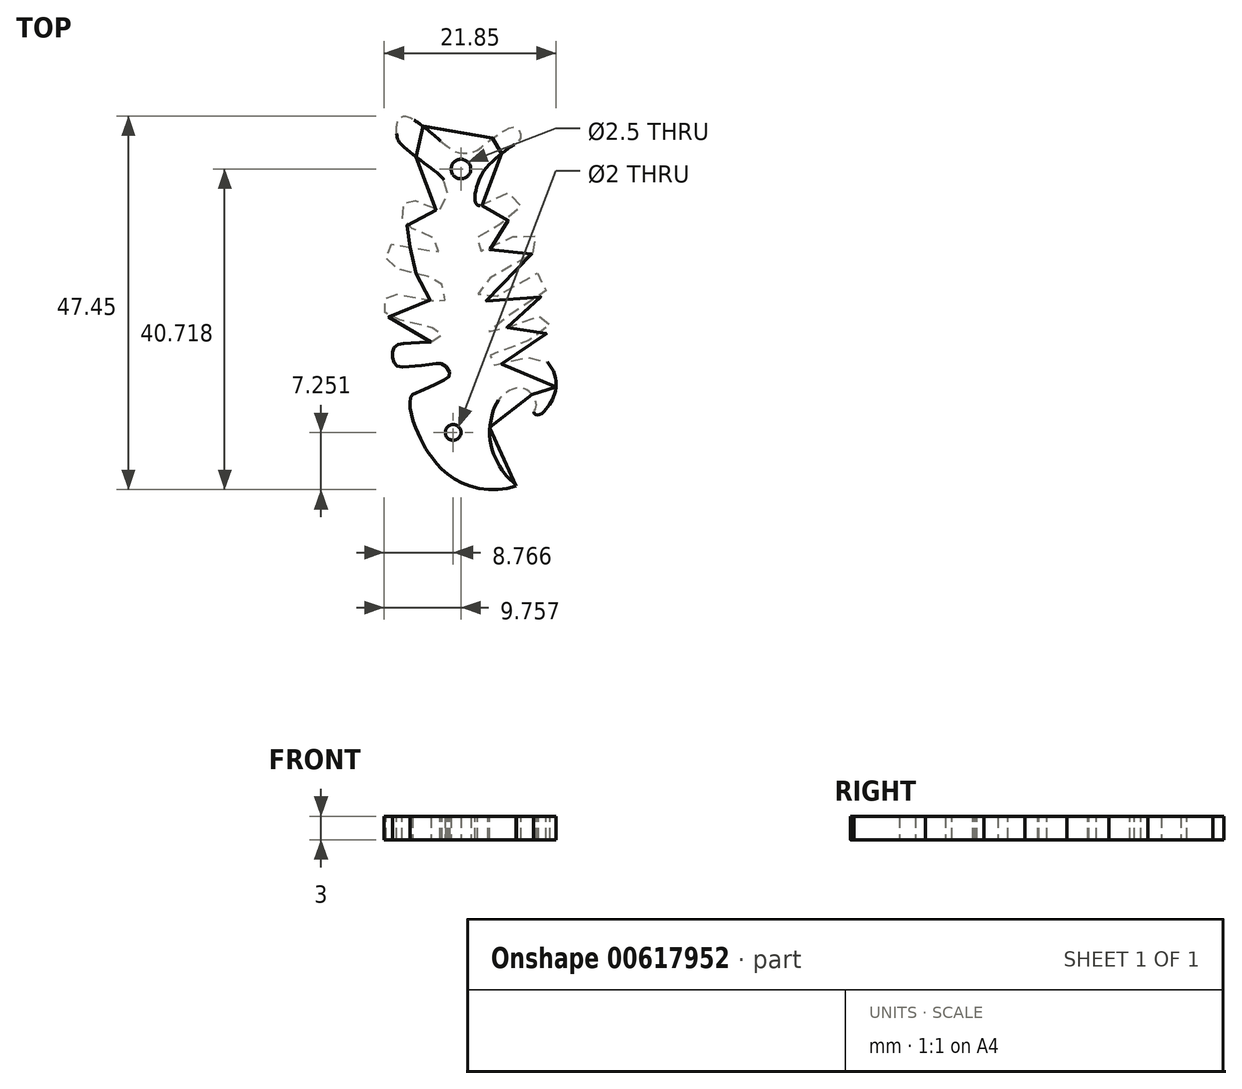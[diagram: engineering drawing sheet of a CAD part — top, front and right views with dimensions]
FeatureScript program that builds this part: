
annotation { "Feature Type Name" : "Feature", "Feature Type Description" : "" }
export const myFeature = defineFeature(function(context is Context, id is Id, definition is map)
    precondition{}
    {
        {
            var Q0;
            Q0=qCreatedBy(makeId("Top.planeOp"),FACE);
            var sketch = newSketch(context, id + "F0", { "sketchPlane" : qUnion([Q0])});
            skFitSpline(sketch, "E0", {"points": [v(6.13, -20.14) * mm, v(-0.93, -19.67) * mm, v(-4.7, -16.3) * mm, v(-6.1, -13.93) * mm, v(-7.28, -10.5) * mm, v(-7.02, -8.5) * mm], "startDerivative": vector(-25.08, -8.24) * mm, "endDerivative": vector(7.76, 5.26) * mm});
            skFitSpline(sketch, "E1", {"points": [v(-7.02, -8.5) * mm, v(-2.72, -6.48) * mm, v(-2.28, -5.84) * mm, v(-3.08, -4.7) * mm, v(-4.22, -4.59) * mm, v(-6.24, -4.86) * mm, v(-7.67, -4.96) * mm, v(-9.04, -4.88) * mm, v(-9.5, -4.1) * mm, v(-9.54, -3.1) * mm, v(-9.16, -2.31) * mm, v(-7.99, -2) * mm, v(-4.66, -1.85) * mm], "startDerivative": vector(31.33, 13.7) * mm, "endDerivative": vector(38.08, 1.18) * mm});
            skFitSpline(sketch, "E2", {"points": [v(-4.66, -1.85) * mm, v(-3.6, -1.52) * mm, v(-3.29, -0.77) * mm, v(-3.8, -0.25) * mm, v(-4.66, 0) * mm, v(-9.7, 1.25) * mm, v(-10.44, 1.63) * mm, v(-10.61, 2.48) * mm, v(-10.55, 3.42) * mm, v(-10.06, 4.3) * mm, v(-9, 4.25) * mm, v(-3.9, 3.3) * mm, v(-3.3, 3.21) * mm, v(-2.83, 3.57) * mm, v(-2.91, 4.8) * mm, v(-3.73, 5.97) * mm, v(-4.96, 6.47) * mm, v(-9.46, 7.6) * mm, v(-10.28, 8.27) * mm, v(-10.32, 9.72) * mm, v(-9.74, 10.6) * mm, v(-8.55, 10.5) * mm, v(-4.28, 9.64) * mm, v(-3.6, 9.76) * mm, v(-3.83, 10.89) * mm, v(-6.15, 12.2) * mm, v(-7.76, 12.99) * mm, v(-8.2, 13.58) * mm, v(-8.35, 14.7) * mm, v(-8.1, 15.88) * mm, v(-7.74, 16.28) * mm, v(-6.82, 16.18) * mm, v(-3.63, 14.93) * mm, v(-2.67, 16.16) * mm, v(-2.56, 17.41) * mm, v(-2.97, 18.62) * mm, v(-3.7, 19.5) * mm, v(-8.27, 23.08) * mm, v(-8.97, 24.2) * mm, v(-9.03, 25.7) * mm, v(-8.5, 26.7) * mm, v(-7.39, 26.7) * mm, v(-2.54, 22.96) * mm, v(-1.18, 22.24) * mm, v(0.65, 22.28) * mm, v(2.37, 23.47) * mm, v(3.96, 24.58) * mm, v(5.35, 25.38) * mm, v(6.34, 25.27) * mm, v(6.7, 24.12) * mm, v(5.48, 22.96) * mm, v(3.52, 21.47) * mm, v(1.67, 19.3) * mm, v(0.94, 16.97) * mm, v(0.94, 16.16) * mm, v(1.14, 15.63) * mm, v(1.91, 15.55) * mm, v(4.71, 16.97) * mm, v(6.04, 17.04) * mm, v(6.75, 15.85) * mm, v(6.2, 14.34) * mm, v(4.06, 13.1) * mm, v(1.93, 12) * mm, v(0.98, 11.17) * mm, v(0.96, 10.5) * mm, v(1.38, 9.88) * mm, v(2.53, 9.78) * mm, v(6.6, 12) * mm, v(8, 12.12) * mm, v(8.86, 11.24) * mm, v(8.86, 9.98) * mm, v(7.65, 9.08) * mm, v(1.9, 5.67) * mm, v(1.34, 5.08) * mm, v(1.26, 4.33) * mm, v(1.75, 3.6) * mm, v(2.59, 3.45) * mm, v(8.28, 6.76) * mm, v(9.42, 6.64) * mm, v(9.94, 5.24) * mm, v(9.32, 3.94) * mm, v(3.02, 0.34) * mm, v(2.65, 0) * mm, v(2.69, -0.5) * mm, v(3.2, -0.6) * mm, v(4.31, -0.22) * mm, v(7.5, 0.88) * mm, v(9.3, 1.53) * mm, v(10, 1.45) * mm, v(10.33, 0.93) * mm, v(10.43, -0.25) * mm, v(10, -0.77) * mm, v(3.28, -3.25) * mm, v(2.78, -3.55) * mm, v(2.6, -3.92) * mm, v(2.69, -4.62) * mm, v(3.5, -4.78) * mm, v(6.91, -3.92) * mm, v(8.5, -3.63) * mm, v(9.54, -3.9) * mm, v(11, -5.89) * mm, v(11.06, -8.3) * mm, v(10.2, -9.99) * mm, v(8.98, -11.08) * mm, v(8.38, -10.82) * mm, v(8.65, -10.23) * mm, v(8.44, -8.92) * mm, v(7.4, -7.89) * mm, v(5.95, -7.76) * mm, v(4.23, -8.8) * mm, v(3.36, -10.27) * mm, v(2.78, -12.7) * mm, v(3.04, -15.34) * mm, v(3.96, -17.44) * mm, v(4.97, -18.93) * mm, v(5.63, -19.55) * mm, v(6.13, -20.14) * mm], "startDerivative": vector(162.9, 22.3) * mm, "endDerivative": vector(-65.49, -30.87) * mm});
            skCircle(sketch, "E3", {"center": v(-0.87, 20.14) * mm, "radius": 1.25 * mm});
            skCircle(sketch, "E4", {"center": v(-1.86, -13.33) * mm, "radius": 1 * mm});
            skSolve(sketch);
        }
        {
            var Q0;
            Q0=makeQuery(id+"F0.imprint","IMPRINT",FACE,{"disambiguationData":[TD([[makeQuery(id+"F0.imprint","IMPRINT",EDGE,{"derivedFrom":sQuery(id+"F0.wireOp",EDGE,"E0")}),-1.0]])]});
            extrude(context, id + "F1", {"entities" : qUnion([Q0]), "depth" : 3 * mm, "offsetDistance" : 25 * mm});
        }
    });
